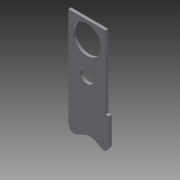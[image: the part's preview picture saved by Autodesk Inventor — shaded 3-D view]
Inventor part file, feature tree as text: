
AUTODESK INVENTOR PART (.ipt)
format: ipt  version: 2015 (Build 190159000, 159)  size: 93,696 bytes
history: native  units: mm
features: extrude x1, sketch x1
ambient origin geometry x8: Origin, YZ Plane, XZ Plane, XY Plane, X Axis, Y Axis, Z Axis, Center Point
bodies: Solid1 (feature_tree)
feature tree (2):
  extrude  "Extrusion1"  Depth=23.5mm
  sketch  "Sketch1"  dims[d0=10.5mm d2=23.5mm d3=21.0mm d4=14.0mm d5=13.0mm d6=28.0mm d7=54.75mm d8=2.5mm d9=20.25mm d10=62.0mm d11=2.0mm d12=0.0mm]
